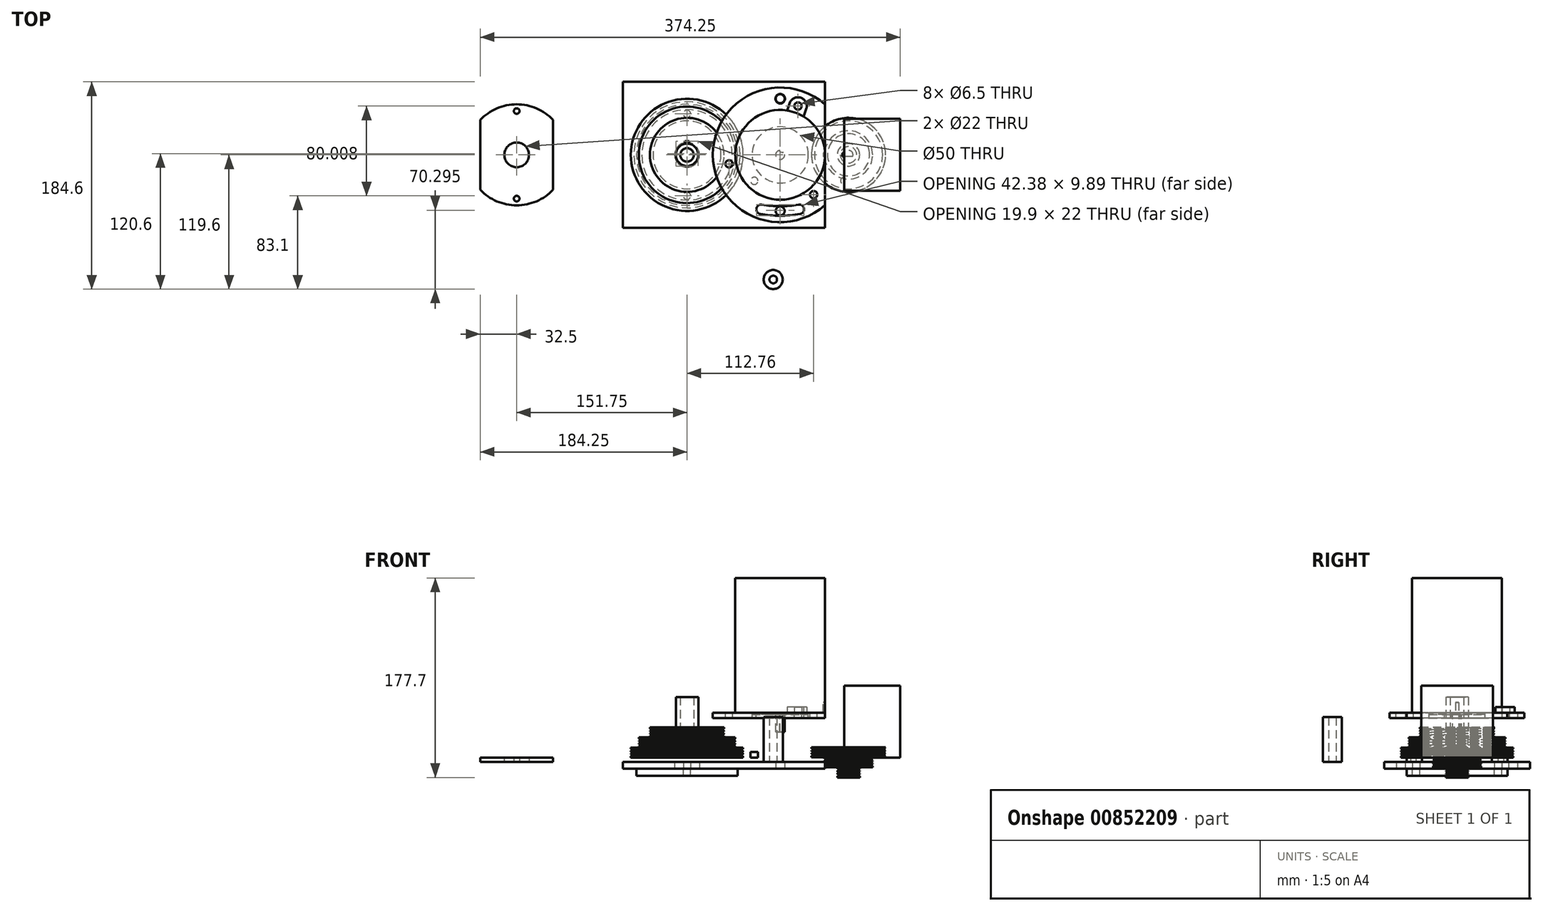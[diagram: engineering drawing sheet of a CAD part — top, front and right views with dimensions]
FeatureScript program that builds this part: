
annotation { "Feature Type Name" : "Feature", "Feature Type Description" : "" }
export const myFeature = defineFeature(function(context is Context, id is Id, definition is map)
    precondition{}
    {
        {
            var Q0;
            Q0=qCreatedBy(makeId("Top.planeOp"),FACE);
            var sketch = newSketch(context, id + "F0", { "sketchPlane" : qUnion([Q0])});
            skCircle(sketch, "E0", {"center": v(0, 0) * mm, "radius": 40 * mm});
            skCircle(sketch, "E1", {"center": v(0, 0) * mm, "radius": 25 * mm});
            skCircle(sketch, "E2", {"center": v(0, 0) * mm, "radius": 46.3 * mm, "construction": true});
            skCircle(sketch, "E3", {"center": v(0, 46.3) * mm, "radius": 3.25 * mm});
            skArc(sketch, "E4", {"start": v(-7.8, 46.3) * mm, "mid": v(0, 54.1) * mm, "end": v(7.8, 46.3) * mm});
            skLineSegment(sketch, "E5", {"start": v(-7.8, 46.3) * mm, "end": v(-7.8, 39.23) * mm});
            skLineSegment(sketch, "E6", {"start": v(7.8, 46.3) * mm, "end": v(7.8, 39.23) * mm});
            skLineSegment(sketch, "E7.1.0", {"start": v(44, -16.4) * mm, "end": v(37.88, -12.86) * mm});
            skLineSegment(sketch, "E7.1.1", {"start": v(36.2, -29.9) * mm, "end": v(30.08, -26.37) * mm});
            skCircle(sketch, "E7.1.2", {"center": v(40.1, -23.15) * mm, "radius": 3.25 * mm});
            skArc(sketch, "E7.1.3", {"start": v(44, -16.4) * mm, "mid": v(46.85, -27.05) * mm, "end": v(36.2, -29.9) * mm});
            skLineSegment(sketch, "E7.2.0", {"start": v(-36.2, -29.9) * mm, "end": v(-30.08, -26.37) * mm});
            skLineSegment(sketch, "E7.2.1", {"start": v(-44, -16.4) * mm, "end": v(-37.88, -12.86) * mm});
            skCircle(sketch, "E7.2.2", {"center": v(-40.1, -23.15) * mm, "radius": 3.25 * mm});
            skArc(sketch, "E7.2.3", {"start": v(-36.2, -29.9) * mm, "mid": v(-46.85, -27.05) * mm, "end": v(-44, -16.4) * mm});
            skLineSegment(sketch, "E7.anchor1", {"start": v(0, 0) * mm, "end": v(0, 46.3) * mm, "construction": true});
            skLineSegment(sketch, "E7.anchor2", {"start": v(0, 0) * mm, "end": v(-40.1, -23.15) * mm, "construction": true});
            skSolve(sketch);
        }
        {
            var Q0;
            Q0=makeQuery(id+"F0.imprint","IMPRINT",FACE,{"disambiguationData":[TD([[makeQuery(id+"F0.imprint","IMPRINT",EDGE,{"derivedFrom":sQuery(id+"F0.wireOp",EDGE,"E1")}),1.0]])]});
            extrude(context, id + "F1", {"entities" : qUnion([Q0]), "oppositeDirection" : true, "depth" : 1.5 * mm, "offsetDistance" : 25 * mm});
        }
        {
            var Q0;
            Q0 = qSketchRegion(id + "F0", true);
            var Q1;
            Q1=makeQuery(id+"F1.opExtrude","CAP_FACE",FACE,{"disambiguationData":[OSD([sQuery(id+"F0.wireOp",EDGE,"E1")])],"isStart":true});
            var Q2;
            Q2=sQuery(id+"F0.wireOp",EDGE,"E0");
            extrude(context, id + "F2", {"entities" : qUnion([Q0, Q1]), "operationType" : NewBodyOperationType.ADD, "surfaceEntities" : qUnion([Q2]), "depth" : 5 * mm, "offsetDistance" : 25 * mm});
        }
        {
            var Q0;
            {var subQ0=sQuery(id+"F0.wireOp",EDGE,"E1");Q0=makeQuery(id+"F2.boolean.opBoolean","MERGE",FACE,{"derivedFrom":[makeQuery(id+"F2.opExtrude","CAP_FACE",FACE,{"disambiguationData":[OSD([sQuery(id+"F0.wireOp",EDGE,"E0"),subQ0,sQuery(id+"F0.wireOp",EDGE,"E3"),sQuery(id+"F0.wireOp",EDGE,"E4"),sQuery(id+"F0.wireOp",EDGE,"E5"),sQuery(id+"F0.wireOp",EDGE,"E6"),sQuery(id+"F0.wireOp",EDGE,"E7.1.0"),sQuery(id+"F0.wireOp",EDGE,"E7.1.1"),sQuery(id+"F0.wireOp",EDGE,"E7.1.2"),sQuery(id+"F0.wireOp",EDGE,"E7.1.3"),sQuery(id+"F0.wireOp",EDGE,"E7.2.0"),sQuery(id+"F0.wireOp",EDGE,"E7.2.1"),sQuery(id+"F0.wireOp",EDGE,"E7.2.2"),sQuery(id+"F0.wireOp",EDGE,"E7.2.3")])],"isStart":false}),makeQuery(id+"F2.opExtrude","CAP_FACE",FACE,{"disambiguationData":[OSD([subQ0])],"isStart":false})]});}
            var sketch = newSketch(context, id + "F3", { "sketchPlane" : qUnion([Q0])});
            skCircle(sketch, "E8", {"center": v(0, 0) * mm, "radius": 40 * mm});
            skSolve(sketch);
        }
        {
            var Q0;
            {var subQ0=sQuery(id+"F3.wireOp",EDGE,"E8");var subQ4=makeQuery(id+"F3.imprint","INTERSECT",VERTEX,{"derivedFrom":[makeQuery(id+"F2.opExtrude","CAP_EDGE",EDGE,{"disambiguationData":[OSD([sQuery(id+"F0.wireOp",EDGE,"E5")])],"isStart":false}),subQ0]});Q0=makeQuery(id+"F3.imprint","IMPRINT",FACE,{"disambiguationData":[TD([[makeQuery(id+"F3.imprint","IMPRINT",EDGE,{"disambiguationData":[TD([[subQ4,1.0]])],"derivedFrom":subQ0}),1.0]])]});}
            extrude(context, id + "F4", {"entities" : qUnion([Q0]), "operationType" : NewBodyOperationType.ADD, "depth" : 115 * mm, "offsetDistance" : 25 * mm});
        }
        {
            var Q0;
            Q0=makeQuery(id+"F1.opExtrude","CAP_FACE",FACE,{"disambiguationData":[OSD([sQuery(id+"F0.wireOp",EDGE,"E1")])],"isStart":false});
            var sketch = newSketch(context, id + "F5", { "sketchPlane" : qUnion([Q0])});
            skArc(sketch, "E9", {"start": v(1.5, -3.7) * mm, "mid": v(0, 4) * mm, "end": v(-1.5, -3.7) * mm});
            skLineSegment(sketch, "E10.bottom", {"start": v(-1.5, -2.5) * mm, "end": v(1.5, -2.5) * mm});
            skLineSegment(sketch, "E10.left", {"start": v(-1.5, -2.5) * mm, "end": v(-1.5, -3.7) * mm});
            skLineSegment(sketch, "E10.right", {"start": v(1.5, -2.5) * mm, "end": v(1.5, -3.7) * mm});
            skSolve(sketch);
        }
        {
            var Q0;
            Q0 = qSketchRegion(id + "F5", true);
            extrude(context, id + "F6", {"entities" : qUnion([Q0]), "operationType" : NewBodyOperationType.ADD, "depth" : 15.7 * mm, "offsetDistance" : 25 * mm});
        }
        {
            var Q0;
            Q0=qCreatedBy(makeId("Top.planeOp"),FACE);
            var sketch = newSketch(context, id + "F7", { "sketchPlane" : qUnion([Q0])});
            skCircle(sketch, "E11", {"center": v(-100, 0) * mm, "radius": 45 * mm});
            skCircle(sketch, "E12", {"center": v(-100, 0) * mm, "radius": 36.5 * mm, "construction": true});
            skCircle(sketch, "E13", {"center": v(-100, 36.5) * mm, "radius": 3.25 * mm});
            skCircle(sketch, "E14", {"center": v(-100, -36.5) * mm, "radius": 3.25 * mm});
            skSolve(sketch);
        }
        {
            var Q0;
            Q0 = qSketchRegion(id + "F7", true);
            extrude(context, id + "F8", {"entities" : qUnion([Q0]), "oppositeDirection" : true, "depth" : 6.3 * mm, "offsetDistance" : 25 * mm});
        }
        {
            var Q0;
            Q0=makeQuery(id+"F8.opExtrude","CAP_FACE",FACE,{"disambiguationData":[OSD([sQuery(id+"F7.wireOp",EDGE,"E11"),sQuery(id+"F7.wireOp",EDGE,"E13"),sQuery(id+"F7.wireOp",EDGE,"E14")])],"isStart":true});
            var sketch = newSketch(context, id + "F9", { "sketchPlane" : qUnion([Q0])});
            skCircle(sketch, "E15", {"center": v(-100, 0) * mm, "radius": 10 * mm});
            skCircle(sketch, "E16", {"center": v(-100, 0) * mm, "radius": 6 * mm});
            skLineSegment(sketch, "E17.bottom", {"start": v(40, 32) * mm, "end": v(90, 32) * mm});
            skLineSegment(sketch, "E17.top", {"start": v(40, -32) * mm, "end": v(90, -32) * mm});
            skLineSegment(sketch, "E17.left", {"start": v(40, 32) * mm, "end": v(40, -32) * mm});
            skLineSegment(sketch, "E17.right", {"start": v(90, 32) * mm, "end": v(90, -32) * mm});
            skPoint(sketch, "E18", {"position": v(40, 0) * mm});
            skSolve(sketch);
        }
        {
            var Q0;
            Q0 = qSketchRegion(id + "F9", true);
            extrude(context, id + "F10", {"entities" : qUnion([Q0]), "operationType" : NewBodyOperationType.ADD, "depth" : 64 * mm, "offsetDistance" : 25 * mm});
        }
        {
            var Q0;
            Q0=makeQuery(id+"F1.opExtrude","SWEPT_BODY",BODY,{"disambiguationData":[OSD([sQuery(id+"F0.wireOp",EDGE,"E1")])]});
            var Q1;
            {var subQ0=sQuery(id+"F0.wireOp",EDGE,"E0");Q1=makeQuery(id+"F4.boolean.opBoolean","MERGE",FACE,{"derivedFrom":[makeQuery(id+"F2.opExtrude","SWEPT_FACE",FACE,{"disambiguationData":[OSD([subQ0]),TDD([makeQuery(id+"F0.imprint","IMPRINT",EDGE,{"disambiguationData":[TD([[makeQuery(id+"F0.imprint","INTERSECT",VERTEX,{"derivedFrom":[subQ0,sQuery(id+"F0.wireOp",EDGE,"E5")]}),-1.0]])],"derivedFrom":subQ0})])]}),makeQuery(id+"F2.opExtrude","SWEPT_FACE",FACE,{"disambiguationData":[OSD([subQ0]),TDD([makeQuery(id+"F0.imprint","IMPRINT",EDGE,{"disambiguationData":[TD([[makeQuery(id+"F0.imprint","INTERSECT",VERTEX,{"derivedFrom":[subQ0,sQuery(id+"F0.wireOp",EDGE,"E7.1.1")]}),1.0]])],"derivedFrom":subQ0})])]}),makeQuery(id+"F2.opExtrude","SWEPT_FACE",FACE,{"disambiguationData":[OSD([subQ0]),TDD([makeQuery(id+"F0.imprint","IMPRINT",EDGE,{"disambiguationData":[TD([[makeQuery(id+"F0.imprint","INTERSECT",VERTEX,{"derivedFrom":[subQ0,sQuery(id+"F0.wireOp",EDGE,"E6")]}),1.0]])],"derivedFrom":subQ0})])]}),makeQuery(id+"F4.opExtrude","SWEPT_FACE",FACE,{"disambiguationData":[OSD([sQuery(id+"F3.wireOp",EDGE,"E8")])]})]});}
            transform(context, id + "F11", {"entities" : qUnion([Q0]), "transformType" : TransformType.ROTATION, "transformAxis" : qUnion([Q1]), "angle" : 20 * degree, "makeCopy" : false});
        }
        {
            var Q0;
            Q0=qCreatedBy(makeId("Front.planeOp"),FACE);
            var sketch = newSketch(context, id + "F12", { "sketchPlane" : qUnion([Q0])});
            skPoint(sketch, "E19.0", {"position": v(-100, 0) * mm});
            skLineSegment(sketch, "E20", {"start": v(-100, 0) * mm, "end": v(-150, 0) * mm});
            skLineSegment(sketch, "E21", {"start": v(-150, 0) * mm, "end": v(-150, 9) * mm});
            skLineSegment(sketch, "E22", {"start": v(-150, 9) * mm, "end": v(-143, 9) * mm});
            skLineSegment(sketch, "E23", {"start": v(-143, 9) * mm, "end": v(-143, 18) * mm});
            skLineSegment(sketch, "E24", {"start": v(-143, 18) * mm, "end": v(-133, 18) * mm});
            skLineSegment(sketch, "E25", {"start": v(-133, 18) * mm, "end": v(-133, 27) * mm});
            skLineSegment(sketch, "E26", {"start": v(-133, 27) * mm, "end": v(-100, 27) * mm});
            skLineSegment(sketch, "E27", {"start": v(-100, 27) * mm, "end": v(-100, 0) * mm});
            skLineSegment(sketch, "E28", {"start": v(-100, 0) * mm, "end": v(-100, 41.1) * mm, "construction": true});
            skLineSegment(sketch, "E29", {"start": v(-143, 16.82) * mm, "end": v(-140.3, 15.84) * mm});
            skLineSegment(sketch, "E30", {"start": v(-140.3, 15.84) * mm, "end": v(-143, 14.86) * mm});
            skLineSegment(sketch, "E31", {"start": v(-143, 14.86) * mm, "end": v(-143, 14.48) * mm});
            skLineSegment(sketch, "E32", {"start": v(-143, 14.48) * mm, "end": v(-140.3, 13.5) * mm});
            skLineSegment(sketch, "E33", {"start": v(-140.3, 13.5) * mm, "end": v(-143, 12.52) * mm});
            skLineSegment(sketch, "E34", {"start": v(-143, 12.52) * mm, "end": v(-143, 12.14) * mm});
            skLineSegment(sketch, "E35", {"start": v(-143, 12.14) * mm, "end": v(-140.3, 11.16) * mm});
            skLineSegment(sketch, "E36", {"start": v(-140.3, 11.16) * mm, "end": v(-143, 10.18) * mm});
            skPoint(sketch, "E37", {"position": v(-143, 13.5) * mm});
            skLineSegment(sketch, "E38", {"start": v(-140.3, 13.5) * mm, "end": v(-143, 13.5) * mm, "construction": true});
            skPoint(sketch, "E39", {"position": v(-133, 22.5) * mm});
            skPoint(sketch, "E40", {"position": v(-150, 4.5) * mm});
            skLineSegment(sketch, "E41", {"start": v(-147.48, 38.86) * mm, "end": v(-144.79, 37.88) * mm});
            skLineSegment(sketch, "E42", {"start": v(-144.79, 37.88) * mm, "end": v(-147.48, 36.9) * mm});
            skLineSegment(sketch, "E43", {"start": v(-147.48, 36.9) * mm, "end": v(-147.48, 36.52) * mm});
            skLineSegment(sketch, "E44", {"start": v(-147.48, 36.52) * mm, "end": v(-144.79, 35.54) * mm});
            skLineSegment(sketch, "E45", {"start": v(-144.79, 35.54) * mm, "end": v(-147.48, 34.56) * mm});
            skLineSegment(sketch, "E46", {"start": v(-147.48, 34.56) * mm, "end": v(-147.48, 34.18) * mm});
            skLineSegment(sketch, "E47", {"start": v(-147.48, 34.18) * mm, "end": v(-144.79, 33.2) * mm});
            skLineSegment(sketch, "E48", {"start": v(-144.79, 33.2) * mm, "end": v(-147.48, 32.22) * mm});
            skPoint(sketch, "E49", {"position": v(-147.48, 35.54) * mm});
            skLineSegment(sketch, "E50", {"start": v(-144.79, 35.54) * mm, "end": v(-147.48, 35.54) * mm, "construction": true});
            skLineSegment(sketch, "E51", {"start": v(-150, 7.82) * mm, "end": v(-147.3, 6.84) * mm});
            skLineSegment(sketch, "E52", {"start": v(-147.3, 6.84) * mm, "end": v(-150, 5.86) * mm});
            skLineSegment(sketch, "E53", {"start": v(-150, 5.86) * mm, "end": v(-150, 5.48) * mm});
            skLineSegment(sketch, "E54", {"start": v(-150, 5.48) * mm, "end": v(-147.3, 4.5) * mm});
            skLineSegment(sketch, "E55", {"start": v(-147.3, 4.5) * mm, "end": v(-150, 3.52) * mm});
            skLineSegment(sketch, "E56", {"start": v(-150, 3.52) * mm, "end": v(-150, 3.14) * mm});
            skLineSegment(sketch, "E57", {"start": v(-150, 3.14) * mm, "end": v(-147.3, 2.16) * mm});
            skLineSegment(sketch, "E58", {"start": v(-147.3, 2.16) * mm, "end": v(-150, 1.18) * mm});
            skLineSegment(sketch, "E59", {"start": v(-147.3, 4.5) * mm, "end": v(-150, 4.5) * mm, "construction": true});
            skLineSegment(sketch, "E60", {"start": v(-133, 25.82) * mm, "end": v(-130.3, 24.84) * mm});
            skLineSegment(sketch, "E61", {"start": v(-130.3, 24.84) * mm, "end": v(-133, 23.86) * mm});
            skLineSegment(sketch, "E62", {"start": v(-133, 23.86) * mm, "end": v(-133, 23.48) * mm});
            skLineSegment(sketch, "E63", {"start": v(-133, 23.48) * mm, "end": v(-130.3, 22.5) * mm});
            skLineSegment(sketch, "E64", {"start": v(-130.3, 22.5) * mm, "end": v(-133, 21.52) * mm});
            skLineSegment(sketch, "E65", {"start": v(-133, 21.52) * mm, "end": v(-133, 21.14) * mm});
            skLineSegment(sketch, "E66", {"start": v(-133, 21.14) * mm, "end": v(-130.3, 20.16) * mm});
            skLineSegment(sketch, "E67", {"start": v(-130.3, 20.16) * mm, "end": v(-133, 19.18) * mm});
            skLineSegment(sketch, "E68", {"start": v(-130.3, 22.5) * mm, "end": v(-133, 22.5) * mm, "construction": true});
            skSolve(sketch);
        }
        {
            var Q0;
            Q0 = qSketchRegion(id + "F12", true);
            var Q1;
            Q1=sQuery(id+"F12.wireOp",EDGE,"E28");
            revolve(context, id + "F13", {"surfaceOperationType" : NewSurfaceOperationType.NEW, "entities" : qUnion([Q0]), "axis" : qUnion([Q1]), "revolveType" : RevolveType.FULL});
        }
        {
            var Q0;
            {var subQ0=sQuery(id+"F12.wireOp",EDGE,"E60");Q0=makeQuery(id+"F12.imprint","IMPRINT",FACE,{"disambiguationData":[TD([[makeQuery(id+"F12.imprint","IMPRINT",EDGE,{"derivedFrom":subQ0}),-1.0]])]});}
            var Q1;
            {var subQ0=sQuery(id+"F12.wireOp",EDGE,"E63");Q1=makeQuery(id+"F12.imprint","IMPRINT",FACE,{"disambiguationData":[TD([[makeQuery(id+"F12.imprint","IMPRINT",EDGE,{"derivedFrom":subQ0}),-1.0]])]});}
            var Q2;
            {var subQ0=sQuery(id+"F12.wireOp",EDGE,"E66");Q2=makeQuery(id+"F12.imprint","IMPRINT",FACE,{"disambiguationData":[TD([[makeQuery(id+"F12.imprint","IMPRINT",EDGE,{"derivedFrom":subQ0}),-1.0]])]});}
            var Q3;
            {var subQ0=sQuery(id+"F12.wireOp",EDGE,"E29");Q3=makeQuery(id+"F12.imprint","IMPRINT",FACE,{"disambiguationData":[TD([[makeQuery(id+"F12.imprint","IMPRINT",EDGE,{"derivedFrom":subQ0}),-1.0]])]});}
            var Q4;
            {var subQ0=sQuery(id+"F12.wireOp",EDGE,"E32");Q4=makeQuery(id+"F12.imprint","IMPRINT",FACE,{"disambiguationData":[TD([[makeQuery(id+"F12.imprint","IMPRINT",EDGE,{"derivedFrom":subQ0}),-1.0]])]});}
            var Q5;
            {var subQ0=sQuery(id+"F12.wireOp",EDGE,"E35");Q5=makeQuery(id+"F12.imprint","IMPRINT",FACE,{"disambiguationData":[TD([[makeQuery(id+"F12.imprint","IMPRINT",EDGE,{"derivedFrom":subQ0}),-1.0]])]});}
            var Q6;
            {var subQ0=sQuery(id+"F12.wireOp",EDGE,"E51");Q6=makeQuery(id+"F12.imprint","IMPRINT",FACE,{"disambiguationData":[TD([[makeQuery(id+"F12.imprint","IMPRINT",EDGE,{"derivedFrom":subQ0}),-1.0]])]});}
            var Q7;
            {var subQ0=sQuery(id+"F12.wireOp",EDGE,"E54");Q7=makeQuery(id+"F12.imprint","IMPRINT",FACE,{"disambiguationData":[TD([[makeQuery(id+"F12.imprint","IMPRINT",EDGE,{"derivedFrom":subQ0}),-1.0]])]});}
            var Q8;
            {var subQ0=sQuery(id+"F12.wireOp",EDGE,"E57");Q8=makeQuery(id+"F12.imprint","IMPRINT",FACE,{"disambiguationData":[TD([[makeQuery(id+"F12.imprint","IMPRINT",EDGE,{"derivedFrom":subQ0}),-1.0]])]});}
            var Q9;
            Q9=sQuery(id+"F12.wireOp",EDGE,"E28");
            revolve(context, id + "F14", {"operationType" : NewBodyOperationType.REMOVE, "surfaceOperationType" : NewSurfaceOperationType.NEW, "entities" : qUnion([Q0, Q1, Q2, Q3, Q4, Q5, Q6, Q7, Q8]), "axis" : qUnion([Q9]), "revolveType" : RevolveType.FULL, "oppositeDirection" : true});
        }
        {
            var Q0;
            Q0=makeQuery(id+"F13.opRevolve","SWEPT_BODY",BODY,{"disambiguationData":[OSD([sQuery(id+"F12.wireOp",EDGE,"E20"),sQuery(id+"F12.wireOp",EDGE,"E21"),sQuery(id+"F12.wireOp",EDGE,"E22"),sQuery(id+"F12.wireOp",EDGE,"E23"),sQuery(id+"F12.wireOp",EDGE,"E24"),sQuery(id+"F12.wireOp",EDGE,"E25"),sQuery(id+"F12.wireOp",EDGE,"E26"),sQuery(id+"F12.wireOp",EDGE,"E27"),sQuery(id+"F12.wireOp",EDGE,"E31"),sQuery(id+"F12.wireOp",EDGE,"E34"),sQuery(id+"F12.wireOp",EDGE,"E53"),sQuery(id+"F12.wireOp",EDGE,"E56"),sQuery(id+"F12.wireOp",EDGE,"E62"),sQuery(id+"F12.wireOp",EDGE,"E65")])]});
            transform(context, id + "F15", {"entities" : qUnion([Q0]), "transformType" : TransformType.TRANSLATION_3D, "dx" : 157 * mm, "dy" : 0 * mm, "dz" : 0 * mm, "makeCopy" : true});
        }
        {
            var Q0;
            Q0=makeQuery(id+"F15.opPattern","COPY",BODY,{"derivedFrom":makeQuery(id+"F13.opRevolve","SWEPT_BODY",BODY,{"disambiguationData":[OSD([sQuery(id+"F12.wireOp",EDGE,"E20"),sQuery(id+"F12.wireOp",EDGE,"E21"),sQuery(id+"F12.wireOp",EDGE,"E22"),sQuery(id+"F12.wireOp",EDGE,"E23"),sQuery(id+"F12.wireOp",EDGE,"E24"),sQuery(id+"F12.wireOp",EDGE,"E25"),sQuery(id+"F12.wireOp",EDGE,"E26"),sQuery(id+"F12.wireOp",EDGE,"E27"),sQuery(id+"F12.wireOp",EDGE,"E31"),sQuery(id+"F12.wireOp",EDGE,"E34"),sQuery(id+"F12.wireOp",EDGE,"E53"),sQuery(id+"F12.wireOp",EDGE,"E56"),sQuery(id+"F12.wireOp",EDGE,"E62"),sQuery(id+"F12.wireOp",EDGE,"E65")])]}),"instanceName":"1"});
            deleteBodies(context, id + "F16", {"entities" : qUnion([Q0])});
        }
        {
            var Q0;
            Q0=qCreatedBy(makeId("Front.planeOp"),FACE);
            var sketch = newSketch(context, id + "F17", { "sketchPlane" : qUnion([Q0])});
            skPoint(sketch, "E69.0", {"position": v(43.87, -17.7) * mm});
            skLineSegment(sketch, "E70", {"start": v(43.87, -17.7) * mm, "end": v(33.87, -17.7) * mm});
            skLineSegment(sketch, "E71", {"start": v(33.87, -17.7) * mm, "end": v(33.87, -8.7) * mm});
            skLineSegment(sketch, "E72", {"start": v(22.37, -8.7) * mm, "end": v(33.87, -8.7) * mm});
            skLineSegment(sketch, "E73", {"start": v(22.37, -8.7) * mm, "end": v(22.37, 0.3) * mm});
            skLineSegment(sketch, "E74", {"start": v(10.87, 0.3) * mm, "end": v(22.37, 0.3) * mm});
            skLineSegment(sketch, "E75", {"start": v(10.87, 0.3) * mm, "end": v(10.87, 9.3) * mm});
            skLineSegment(sketch, "E76", {"start": v(10.87, 9.3) * mm, "end": v(43.87, 9.3) * mm});
            skLineSegment(sketch, "E77", {"start": v(43.87, 9.3) * mm, "end": v(43.87, -17.7) * mm});
            skLineSegment(sketch, "E78", {"start": v(43.87, -17.7) * mm, "end": v(43.87, 23.39) * mm, "construction": true});
            skLineSegment(sketch, "E79", {"start": v(22.37, -0.89) * mm, "end": v(25.06, -1.87) * mm});
            skLineSegment(sketch, "E80", {"start": v(25.06, -1.87) * mm, "end": v(22.37, -2.85) * mm});
            skLineSegment(sketch, "E81", {"start": v(22.37, -2.85) * mm, "end": v(22.37, -3.23) * mm});
            skLineSegment(sketch, "E82", {"start": v(22.37, -3.23) * mm, "end": v(25.06, -4.2) * mm});
            skLineSegment(sketch, "E83", {"start": v(25.06, -4.2) * mm, "end": v(22.37, -5.19) * mm});
            skLineSegment(sketch, "E84", {"start": v(22.37, -5.19) * mm, "end": v(22.37, -5.57) * mm});
            skLineSegment(sketch, "E85", {"start": v(22.37, -5.57) * mm, "end": v(25.06, -6.55) * mm});
            skLineSegment(sketch, "E86", {"start": v(25.06, -6.55) * mm, "end": v(22.37, -7.53) * mm});
            skPoint(sketch, "E87", {"position": v(22.37, -4.2) * mm});
            skLineSegment(sketch, "E88", {"start": v(25.06, -4.2) * mm, "end": v(22.37, -4.2) * mm, "construction": true});
            skPoint(sketch, "E89", {"position": v(10.87, 4.8) * mm});
            skPoint(sketch, "E90", {"position": v(33.87, -13.2) * mm});
            skLineSegment(sketch, "E91", {"start": v(-3.6, 21.16) * mm, "end": v(-0.92, 20.18) * mm});
            skLineSegment(sketch, "E92", {"start": v(-0.92, 20.18) * mm, "end": v(-3.6, 19.2) * mm});
            skLineSegment(sketch, "E93", {"start": v(-3.6, 19.2) * mm, "end": v(-3.6, 18.82) * mm});
            skLineSegment(sketch, "E94", {"start": v(-3.6, 18.82) * mm, "end": v(-0.92, 17.84) * mm});
            skLineSegment(sketch, "E95", {"start": v(-0.92, 17.84) * mm, "end": v(-3.6, 16.86) * mm});
            skLineSegment(sketch, "E96", {"start": v(-3.6, 16.86) * mm, "end": v(-3.6, 16.48) * mm});
            skLineSegment(sketch, "E97", {"start": v(-3.6, 16.48) * mm, "end": v(-0.92, 15.5) * mm});
            skLineSegment(sketch, "E98", {"start": v(-0.92, 15.5) * mm, "end": v(-3.6, 14.52) * mm});
            skPoint(sketch, "E99", {"position": v(-3.6, 17.84) * mm});
            skLineSegment(sketch, "E100", {"start": v(-0.92, 17.84) * mm, "end": v(-3.6, 17.84) * mm, "construction": true});
            skLineSegment(sketch, "E101", {"start": v(33.87, -9.89) * mm, "end": v(36.56, -10.87) * mm});
            skLineSegment(sketch, "E102", {"start": v(36.56, -10.87) * mm, "end": v(33.87, -11.85) * mm});
            skLineSegment(sketch, "E103", {"start": v(33.87, -11.85) * mm, "end": v(33.87, -12.23) * mm});
            skLineSegment(sketch, "E104", {"start": v(33.87, -12.23) * mm, "end": v(36.56, -13.2) * mm});
            skLineSegment(sketch, "E105", {"start": v(36.56, -13.2) * mm, "end": v(33.87, -14.19) * mm});
            skLineSegment(sketch, "E106", {"start": v(33.87, -14.19) * mm, "end": v(33.87, -14.57) * mm});
            skLineSegment(sketch, "E107", {"start": v(33.87, -14.57) * mm, "end": v(36.56, -15.55) * mm});
            skLineSegment(sketch, "E108", {"start": v(36.56, -15.55) * mm, "end": v(33.87, -16.53) * mm});
            skLineSegment(sketch, "E109", {"start": v(36.56, -13.2) * mm, "end": v(33.87, -13.2) * mm, "construction": true});
            skLineSegment(sketch, "E110", {"start": v(10.87, 8.11) * mm, "end": v(13.56, 7.13) * mm});
            skLineSegment(sketch, "E111", {"start": v(13.56, 7.13) * mm, "end": v(10.87, 6.15) * mm});
            skLineSegment(sketch, "E112", {"start": v(10.87, 6.15) * mm, "end": v(10.87, 5.77) * mm});
            skLineSegment(sketch, "E113", {"start": v(10.87, 5.77) * mm, "end": v(13.56, 4.8) * mm});
            skLineSegment(sketch, "E114", {"start": v(13.56, 4.8) * mm, "end": v(10.87, 3.81) * mm});
            skLineSegment(sketch, "E115", {"start": v(10.87, 3.81) * mm, "end": v(10.87, 3.43) * mm});
            skLineSegment(sketch, "E116", {"start": v(10.87, 3.43) * mm, "end": v(13.56, 2.45) * mm});
            skLineSegment(sketch, "E117", {"start": v(13.56, 2.45) * mm, "end": v(10.87, 1.47) * mm});
            skLineSegment(sketch, "E118", {"start": v(13.56, 4.8) * mm, "end": v(10.87, 4.8) * mm, "construction": true});
            skSolve(sketch);
        }
        {
            var Q0;
            {var subQ7=sQuery(id+"F17.wireOp",EDGE,"E70");Q0=makeQuery(id+"F17.imprint","IMPRINT",FACE,{"disambiguationData":[TD([[makeQuery(id+"F17.imprint","IMPRINT",EDGE,{"derivedFrom":subQ7}),-1.0]])]});}
            var Q1;
            Q1=sQuery(id+"F17.wireOp",EDGE,"E78");
            revolve(context, id + "F18", {"surfaceOperationType" : NewSurfaceOperationType.NEW, "entities" : qUnion([Q0]), "axis" : qUnion([Q1]), "revolveType" : RevolveType.FULL});
        }
        {
            var Q0;
            Q0=makeQuery(id+"F18.opRevolve","SWEPT_FACE",FACE,{"disambiguationData":[OSD([sQuery(id+"F17.wireOp",EDGE,"E76")])]});
            var sketch = newSketch(context, id + "F19", { "sketchPlane" : qUnion([Q0])});
            skCircle(sketch, "E119", {"center": v(43.87, 0) * mm, "radius": 4 * mm});
            skLineSegment(sketch, "E120.bottom", {"start": v(49.37, 1.5) * mm, "end": v(38.37, 1.5) * mm});
            skLineSegment(sketch, "E120.top", {"start": v(49.37, -1.5) * mm, "end": v(38.37, -1.5) * mm});
            skLineSegment(sketch, "E120.left", {"start": v(49.37, 1.5) * mm, "end": v(49.37, -1.5) * mm});
            skLineSegment(sketch, "E120.right", {"start": v(38.37, 1.5) * mm, "end": v(38.37, -1.5) * mm});
            skSolve(sketch);
        }
        {
            var Q0;
            {var subQ0=sQuery(id+"F19.wireOp",EDGE,"E120.top");var subQ1=sQuery(id+"F19.wireOp",EDGE,"E119");var subQ2=makeQuery(id+"F19.imprint","INTERSECT",VERTEX,{"disambiguationData":[OD(0.0)],"derivedFrom":[subQ1,subQ0]});Q0=makeQuery(id+"F19.imprint","IMPRINT",FACE,{"disambiguationData":[TD([[makeQuery(id+"F19.imprint","IMPRINT",EDGE,{"disambiguationData":[TD([[subQ2,-1.0]])],"derivedFrom":subQ1}),1.0]])]});}
            var Q1;
            {var subQ5=sQuery(id+"F19.wireOp",EDGE,"E120.right");Q1=makeQuery(id+"F19.imprint","IMPRINT",FACE,{"disambiguationData":[TD([[makeQuery(id+"F19.imprint","IMPRINT",EDGE,{"derivedFrom":subQ5}),1.0]])]});}
            var Q2;
            {var subQ0=sQuery(id+"F19.wireOp",EDGE,"E120.bottom");var subQ1=sQuery(id+"F19.wireOp",EDGE,"E119");var subQ2=makeQuery(id+"F19.imprint","INTERSECT",VERTEX,{"disambiguationData":[OD(0.0)],"derivedFrom":[subQ1,subQ0]});Q2=makeQuery(id+"F19.imprint","IMPRINT",FACE,{"disambiguationData":[TD([[makeQuery(id+"F19.imprint","IMPRINT",EDGE,{"disambiguationData":[TD([[subQ2,-1.0]])],"derivedFrom":subQ1}),1.0]])]});}
            var Q3;
            {var subQ0=sQuery(id+"F19.wireOp",EDGE,"E120.bottom");var subQ1=sQuery(id+"F19.wireOp",EDGE,"E119");var subQ2=makeQuery(id+"F19.imprint","INTERSECT",VERTEX,{"disambiguationData":[OD(0.0)],"derivedFrom":[subQ1,subQ0]});Q3=makeQuery(id+"F19.imprint","IMPRINT",FACE,{"disambiguationData":[TD([[makeQuery(id+"F19.imprint","IMPRINT",EDGE,{"disambiguationData":[TD([[subQ2,1.0]])],"derivedFrom":subQ1}),1.0]])]});}
            var Q4;
            Q4=makeQuery(id+"F18.opRevolve","SWEPT_FACE",FACE,{"disambiguationData":[OSD([sQuery(id+"F17.wireOp",EDGE,"E70")])]});
            extrude(context, id + "F20", {"entities" : qUnion([Q0, Q1, Q2, Q3]), "operationType" : NewBodyOperationType.REMOVE, "endBound" : BoundingType.UP_TO_SURFACE, "oppositeDirection" : true, "depth" : 25 * mm, "endBoundEntityFace" : qUnion([Q4]), "offsetDistance" : 25 * mm});
        }
        {
            var Q0;
            Q0=makeQuery(id+"F13.opRevolve","SWEPT_FACE",FACE,{"disambiguationData":[OSD([sQuery(id+"F12.wireOp",EDGE,"E26")])]});
            var sketch = newSketch(context, id + "F21", { "sketchPlane" : qUnion([Q0])});
            skCircle(sketch, "E121", {"center": v(-100, 0) * mm, "radius": 10 * mm});
            skLineSegment(sketch, "E122.bottom", {"start": v(-98, -12) * mm, "end": v(-102, -12) * mm});
            skLineSegment(sketch, "E122.top", {"start": v(-98, 12) * mm, "end": v(-102, 12) * mm});
            skLineSegment(sketch, "E122.left", {"start": v(-98, -12) * mm, "end": v(-98, 12) * mm});
            skLineSegment(sketch, "E122.right", {"start": v(-102, -12) * mm, "end": v(-102, 12) * mm});
            skSolve(sketch);
        }
        {
            var Q0;
            {var subQ0=sQuery(id+"F21.wireOp",EDGE,"E122.left");var subQ1=sQuery(id+"F21.wireOp",EDGE,"E121");var subQ2=makeQuery(id+"F21.imprint","INTERSECT",VERTEX,{"disambiguationData":[OD(0.0)],"derivedFrom":[subQ1,subQ0]});Q0=makeQuery(id+"F21.imprint","IMPRINT",FACE,{"disambiguationData":[TD([[makeQuery(id+"F21.imprint","IMPRINT",EDGE,{"disambiguationData":[TD([[subQ2,1.0]])],"derivedFrom":subQ1}),1.0]])]});}
            var Q1;
            {var subQ0=sQuery(id+"F21.wireOp",EDGE,"E122.right");var subQ1=sQuery(id+"F21.wireOp",EDGE,"E121");var subQ2=makeQuery(id+"F21.imprint","INTERSECT",VERTEX,{"disambiguationData":[OD(0.0)],"derivedFrom":[subQ1,subQ0]});Q1=makeQuery(id+"F21.imprint","IMPRINT",FACE,{"disambiguationData":[TD([[makeQuery(id+"F21.imprint","IMPRINT",EDGE,{"disambiguationData":[TD([[subQ2,1.0]])],"derivedFrom":subQ1}),1.0]])]});}
            var Q2;
            {var subQ0=sQuery(id+"F21.wireOp",EDGE,"E122.right");var subQ1=sQuery(id+"F21.wireOp",EDGE,"E121");var subQ2=makeQuery(id+"F21.imprint","INTERSECT",VERTEX,{"disambiguationData":[OD(0.0)],"derivedFrom":[subQ1,subQ0]});Q2=makeQuery(id+"F21.imprint","IMPRINT",FACE,{"disambiguationData":[TD([[makeQuery(id+"F21.imprint","IMPRINT",EDGE,{"disambiguationData":[TD([[subQ2,-1.0]])],"derivedFrom":subQ1}),1.0]])]});}
            var Q3;
            {var subQ5=sQuery(id+"F21.wireOp",EDGE,"E122.top");Q3=makeQuery(id+"F21.imprint","IMPRINT",FACE,{"disambiguationData":[TD([[makeQuery(id+"F21.imprint","IMPRINT",EDGE,{"derivedFrom":subQ5}),1.0]])]});}
            var Q4;
            Q4=makeQuery(id+"F13.opRevolve","SWEPT_FACE",FACE,{"disambiguationData":[OSD([sQuery(id+"F12.wireOp",EDGE,"E20")])]});
            extrude(context, id + "F22", {"entities" : qUnion([Q0, Q1, Q2, Q3]), "operationType" : NewBodyOperationType.REMOVE, "endBound" : BoundingType.UP_TO_SURFACE, "oppositeDirection" : true, "depth" : 25 * mm, "endBoundEntityFace" : qUnion([Q4]), "offsetDistance" : 25 * mm});
        }
        {
            var Q0;
            Q0=makeQuery(id+"F1.opExtrude","SWEPT_BODY",BODY,{"disambiguationData":[OSD([sQuery(id+"F0.wireOp",EDGE,"E1")])]});
            transform(context, id + "F23", {"entities" : qUnion([Q0]), "transformType" : TransformType.TRANSLATION_3D, "dx" : -17 * mm, "dy" : 0 * mm, "dz" : 40 * mm, "makeCopy" : false});
        }
        {
            var Q0;
            Q0=makeQuery(id+"F8.opExtrude","SWEPT_BODY",BODY,{"disambiguationData":[OSD([sQuery(id+"F7.wireOp",EDGE,"E11"),sQuery(id+"F7.wireOp",EDGE,"E13"),sQuery(id+"F7.wireOp",EDGE,"E14")])]});
            transform(context, id + "F24", {"entities" : qUnion([Q0]), "transformType" : TransformType.TRANSLATION_3D, "dx" : 0 * mm, "dy" : 0 * mm, "dz" : -10 * mm, "makeCopy" : false});
        }
        {
            var Q0;
            {var subQ0=sQuery(id+"F0.wireOp",EDGE,"E1");Q0=makeQuery(id+"F2.boolean.opBoolean","MERGE",FACE,{"derivedFrom":[makeQuery(id+"F2.opExtrude","CAP_FACE",FACE,{"disambiguationData":[OSD([sQuery(id+"F0.wireOp",EDGE,"E0"),subQ0,sQuery(id+"F0.wireOp",EDGE,"E3"),sQuery(id+"F0.wireOp",EDGE,"E4"),sQuery(id+"F0.wireOp",EDGE,"E5"),sQuery(id+"F0.wireOp",EDGE,"E6"),sQuery(id+"F0.wireOp",EDGE,"E7.1.0"),sQuery(id+"F0.wireOp",EDGE,"E7.1.1"),sQuery(id+"F0.wireOp",EDGE,"E7.1.2"),sQuery(id+"F0.wireOp",EDGE,"E7.1.3"),sQuery(id+"F0.wireOp",EDGE,"E7.2.0"),sQuery(id+"F0.wireOp",EDGE,"E7.2.1"),sQuery(id+"F0.wireOp",EDGE,"E7.2.2"),sQuery(id+"F0.wireOp",EDGE,"E7.2.3")])],"isStart":true}),makeQuery(id+"F2.opExtrude","CAP_FACE",FACE,{"disambiguationData":[OSD([subQ0])],"isStart":true})]});}
            var sketch = newSketch(context, id + "F25", { "sketchPlane" : qUnion([Q0])});
            skCircle(sketch, "E123.0", {"center": v(-17, 0) * mm, "radius": 25 * mm});
            skCircle(sketch, "E124.0", {"center": v(12.76, 35.47) * mm, "radius": 3.25 * mm});
            skCircle(sketch, "E125.0", {"center": v(-62.6, 8.04) * mm, "radius": 3.25 * mm});
            skCircle(sketch, "E126.0", {"center": v(-1.16, -43.5) * mm, "radius": 3.25 * mm});
            skArc(sketch, "E127.0", {"start": v(-10.91, -39.53) * mm, "mid": v(-42.71, -30.64) * mm, "end": v(-57, -0.87) * mm, "construction": true});
            skArc(sketch, "E128.0", {"start": v(-54.28, 14.5) * mm, "mid": v(-30.68, 37.59) * mm, "end": v(2.24, 35.07) * mm, "construction": true});
            skArc(sketch, "E129.0", {"start": v(14.2, 25.04) * mm, "mid": v(22.4, -6.95) * mm, "end": v(3.75, -34.2) * mm, "construction": true});
            skArc(sketch, "E130", {"start": v(23, 44.72) * mm, "mid": v(-77, 0) * mm, "end": v(23, -44.72) * mm});
            skLineSegment(sketch, "E131", {"start": v(-17, 0) * mm, "end": v(-17, -67.15) * mm, "construction": true});
            skCircle(sketch, "E132", {"center": v(-17, -50) * mm, "radius": 8.5 * mm, "construction": true});
            skCircle(sketch, "E133", {"center": v(-17, -50) * mm, "radius": 4.25 * mm});
            skLineSegment(sketch, "E134", {"start": v(23, -44.72) * mm, "end": v(23, 44.72) * mm});
            skArc(sketch, "E135", {"start": v(-34, 48.54) * mm, "mid": v(-17, 50) * mm, "end": v(0, 48.54) * mm, "construction": true});
            skArc(sketch, "E136.0.startCap", {"start": v(-33.28, 44.36) * mm, "mid": v(-38.19, 47.82) * mm, "end": v(-34.72, 52.73) * mm});
            skArc(sketch, "E136.0.endCap", {"start": v(0.72, 52.73) * mm, "mid": v(4.19, 47.82) * mm, "end": v(-0.72, 44.36) * mm});
            skArc(sketch, "E136.0.left", {"start": v(-34.72, 52.73) * mm, "mid": v(-17, 54.25) * mm, "end": v(0.72, 52.73) * mm});
            skArc(sketch, "E136.0.right", {"start": v(-33.28, 44.36) * mm, "mid": v(-17, 45.75) * mm, "end": v(-0.72, 44.36) * mm});
            skSolve(sketch);
        }
        {
            var Q0;
            Q0 = qSketchRegion(id + "F25", true);
            extrude(context, id + "F26", {"entities" : qUnion([Q0]), "depth" : 4.7 * mm, "offsetDistance" : 25 * mm});
        }
        {
            var Q0;
            {var subQ0=sQuery(id+"F7.wireOp",EDGE,"E11");var subQ1=sQuery(id+"F7.wireOp",EDGE,"E13");var subQ2=sQuery(id+"F7.wireOp",EDGE,"E14");Q0=makeQuery(id+"F10.boolean.opBoolean","SPLIT",FACE,{"disambiguationData":[TD([makeQuery(id+"F8.opExtrude","SWEPT_FACE",FACE,{"disambiguationData":[OSD([subQ0])]})])],"derivedFrom":makeQuery(id+"F8.opExtrude","CAP_FACE",FACE,{"disambiguationData":[OSD([subQ0,subQ1,subQ2])],"isStart":true})});}
            var sketch = newSketch(context, id + "F27", { "sketchPlane" : qUnion([Q0])});
            skLineSegment(sketch, "E137.bottom", {"start": v(23, 65) * mm, "end": v(-157, 65) * mm});
            skLineSegment(sketch, "E137.top", {"start": v(23, -65) * mm, "end": v(-157, -65) * mm});
            skLineSegment(sketch, "E137.left", {"start": v(23, 65) * mm, "end": v(23, -65) * mm});
            skLineSegment(sketch, "E137.right", {"start": v(-157, 65) * mm, "end": v(-157, -65) * mm});
            skCircle(sketch, "E138.0", {"center": v(-100, 36.5) * mm, "radius": 3.25 * mm});
            skCircle(sketch, "E139.0", {"center": v(-100, -36.5) * mm, "radius": 3.25 * mm});
            skPoint(sketch, "E140.0", {"position": v(-100, 0) * mm});
            skCircle(sketch, "E141", {"center": v(-100, 0) * mm, "radius": 11 * mm});
            skPoint(sketch, "E142.0", {"position": v(-17, 50) * mm});
            skCircle(sketch, "E143", {"center": v(-17, 50) * mm, "radius": 4 * mm});
            skCircle(sketch, "E144", {"center": v(-17, -50) * mm, "radius": 4 * mm});
            skPoint(sketch, "E145", {"position": v(23, 0) * mm});
            skLineSegment(sketch, "E146.0", {"start": v(23, 44.72) * mm, "end": v(23, -44.72) * mm, "construction": true});
            skCircle(sketch, "E147", {"center": v(-100, 0) * mm, "radius": 45 * mm, "construction": true});
            skSolve(sketch);
        }
        {
            var Q0;
            Q0 = qSketchRegion(id + "F27", true);
            extrude(context, id + "F28", {"entities" : qUnion([Q0]), "depth" : 6 * mm, "offsetDistance" : 25 * mm});
        }
        {
            var Q0;
            Q0=makeQuery(id+"F28.opExtrude","CAP_FACE",FACE,{"disambiguationData":[OSD([sQuery(id+"F27.wireOp",EDGE,"E137.bottom"),sQuery(id+"F27.wireOp",EDGE,"E137.top"),sQuery(id+"F27.wireOp",EDGE,"E137.left"),sQuery(id+"F27.wireOp",EDGE,"E137.right"),sQuery(id+"F27.wireOp",EDGE,"E138.0"),sQuery(id+"F27.wireOp",EDGE,"E139.0"),sQuery(id+"F27.wireOp",EDGE,"E141"),sQuery(id+"F27.wireOp",EDGE,"E143"),sQuery(id+"F27.wireOp",EDGE,"E144")])],"isStart":false});
            var sketch = newSketch(context, id + "F29", { "sketchPlane" : qUnion([Q0])});
            skCircle(sketch, "E148", {"center": v(-23.24, -111.1) * mm, "radius": 8.5 * mm});
            skCircle(sketch, "E149", {"center": v(-23.24, -111.1) * mm, "radius": 3.38 * mm});
            skSolve(sketch);
        }
        {
            var Q0;
            Q0 = qSketchRegion(id + "F29", true);
            extrude(context, id + "F30", {"entities" : qUnion([Q0]), "depth" : 40 * mm, "offsetDistance" : 25 * mm});
        }
        {
            var Q0;
            Q0=makeQuery(id+"F28.opExtrude","CAP_FACE",FACE,{"disambiguationData":[OSD([sQuery(id+"F27.wireOp",EDGE,"E137.bottom"),sQuery(id+"F27.wireOp",EDGE,"E137.top"),sQuery(id+"F27.wireOp",EDGE,"E137.left"),sQuery(id+"F27.wireOp",EDGE,"E137.right"),sQuery(id+"F27.wireOp",EDGE,"E138.0"),sQuery(id+"F27.wireOp",EDGE,"E139.0"),sQuery(id+"F27.wireOp",EDGE,"E141"),sQuery(id+"F27.wireOp",EDGE,"E143"),sQuery(id+"F27.wireOp",EDGE,"E144")])],"isStart":false});
            var sketch = newSketch(context, id + "F31", { "sketchPlane" : qUnion([Q0])});
            skArc(sketch, "E150", {"start": v(-284.25, -31.12) * mm, "mid": v(-251.75, -45) * mm, "end": v(-219.25, -31.12) * mm});
            skLineSegment(sketch, "E151", {"start": v(-219.25, 31.12) * mm, "end": v(-219.25, -31.12) * mm});
            skLineSegment(sketch, "E152", {"start": v(-284.25, 31.12) * mm, "end": v(-284.25, -31.12) * mm});
            skCircle(sketch, "E153", {"center": v(-251.75, 0) * mm, "radius": 39 * mm, "construction": true});
            skCircle(sketch, "E154", {"center": v(-251.75, -39) * mm, "radius": 2.5 * mm});
            skCircle(sketch, "E155", {"center": v(-251.75, 39) * mm, "radius": 2.5 * mm});
            skArc(sketch, "E156.trimOffspring", {"start": v(-219.25, 31.12) * mm, "mid": v(-251.75, 45) * mm, "end": v(-284.25, 31.12) * mm});
            skCircle(sketch, "E157", {"center": v(-251.75, 0) * mm, "radius": 11 * mm});
            skSolve(sketch);
        }
        {
            var Q0;
            Q0 = qSketchRegion(id + "F31", true);
            extrude(context, id + "F32", {"entities" : qUnion([Q0]), "depth" : 4 * mm, "offsetDistance" : 25 * mm});
        }
    });
